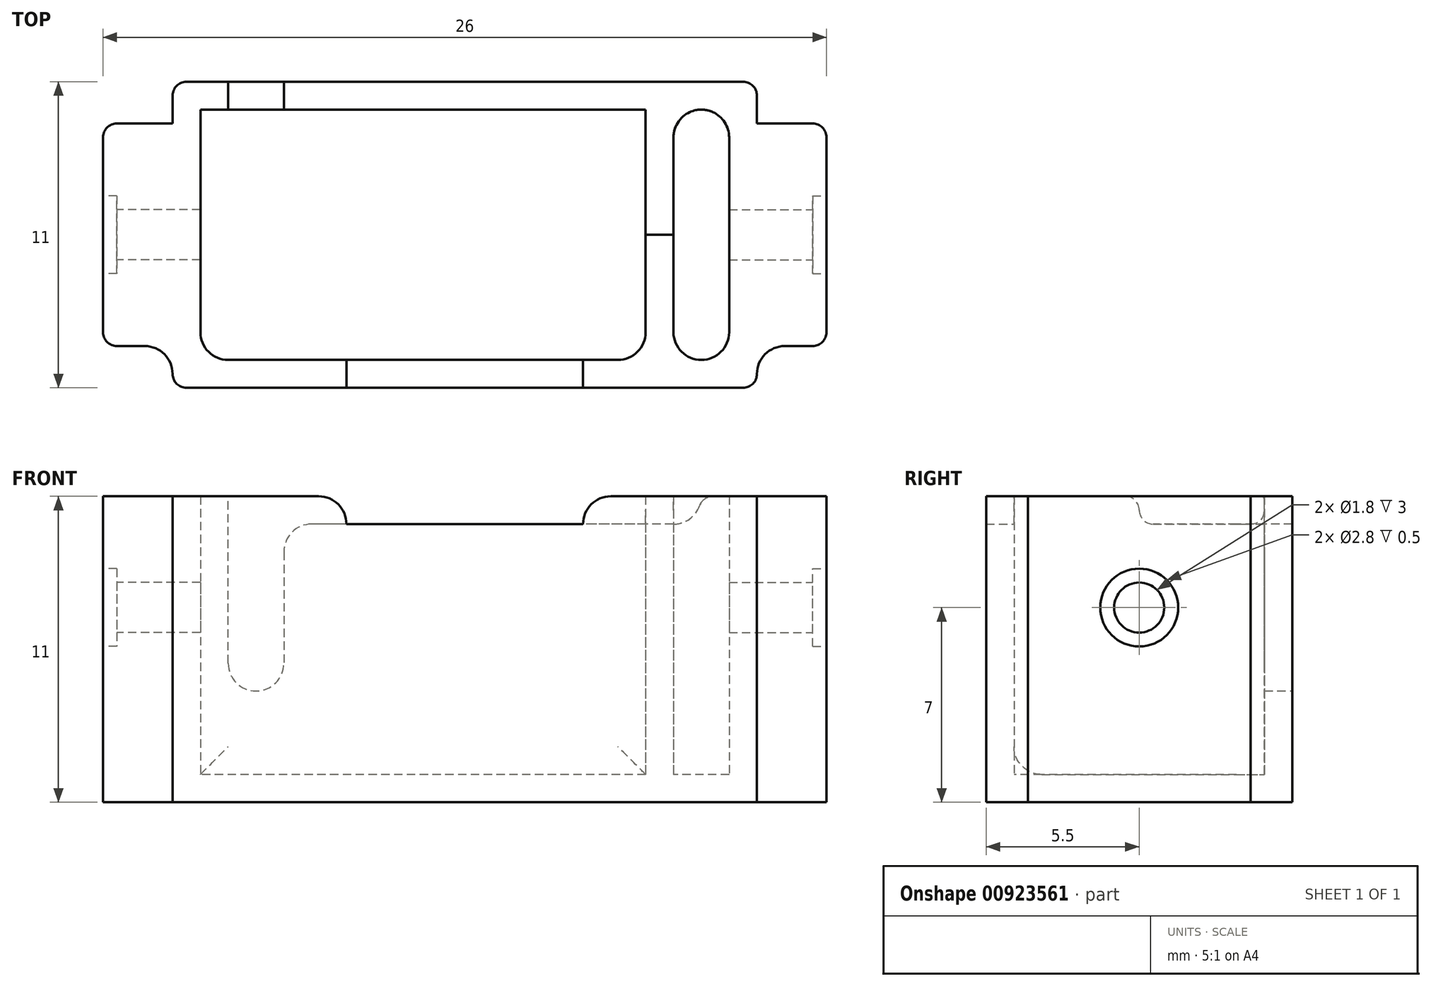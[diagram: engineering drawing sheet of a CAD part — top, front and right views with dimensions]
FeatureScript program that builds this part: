
annotation { "Feature Type Name" : "Feature", "Feature Type Description" : "" }
export const myFeature = defineFeature(function(context is Context, id is Id, definition is map)
    precondition{}
    {
        {
            var Q0;
            Q0=qCreatedBy(makeId("Top.planeOp"),FACE);
            var sketch = newSketch(context, id + "F0", { "sketchPlane" : qUnion([Q0])});
            skLineSegment(sketch, "E0.bottom", {"start": v(9.5, -4.5) * mm, "end": v(-9.5, -4.5) * mm});
            skLineSegment(sketch, "E0.top", {"start": v(9.5, 4.5) * mm, "end": v(-9.5, 4.5) * mm});
            skLineSegment(sketch, "E0.left", {"start": v(9.5, -4.5) * mm, "end": v(9.5, 4.5) * mm});
            skLineSegment(sketch, "E0.right", {"start": v(-9.5, -4.5) * mm, "end": v(-9.5, 4.5) * mm});
            skPoint(sketch, "E0.middle", {"position": v(0, 0) * mm});
            skLineSegment(sketch, "E1.bottom", {"start": v(10.5, -5.5) * mm, "end": v(-10.5, -5.5) * mm});
            skLineSegment(sketch, "E1.top", {"start": v(10.5, 5.5) * mm, "end": v(-10.5, 5.5) * mm});
            skLineSegment(sketch, "E1.left", {"start": v(10.5, -5.5) * mm, "end": v(10.5, 5.5) * mm});
            skLineSegment(sketch, "E1.right", {"start": v(-10.5, -5.5) * mm, "end": v(-10.5, 5.5) * mm});
            skLineSegment(sketch, "E2", {"start": v(9.5, -4.5) * mm, "end": v(6.5, -4.5) * mm});
            skLineSegment(sketch, "E3", {"start": v(6.5, -4.5) * mm, "end": v(6.5, 4.5) * mm});
            skLineSegment(sketch, "E4", {"start": v(13, 0) * mm, "end": v(13, -4) * mm});
            skLineSegment(sketch, "E5", {"start": v(13, -4) * mm, "end": v(10.5, -4) * mm});
            skLineSegment(sketch, "E6", {"start": v(13, 0) * mm, "end": v(13, 4) * mm});
            skLineSegment(sketch, "E7", {"start": v(13, 4) * mm, "end": v(10.5, 4) * mm});
            skLineSegment(sketch, "E8.MirrorCS", {"start": v(-13, 4) * mm, "end": v(-10.5, 4) * mm});
            skLineSegment(sketch, "E9.MirrorCS", {"start": v(-13, 0) * mm, "end": v(-13, 4) * mm});
            skLineSegment(sketch, "E10.MirrorCS", {"start": v(-13, 0) * mm, "end": v(-13, -4) * mm});
            skLineSegment(sketch, "E11.MirrorCS", {"start": v(-13, -4) * mm, "end": v(-10.5, -4) * mm});
            skLineSegment(sketch, "E12", {"start": v(6.5, 4.5) * mm, "end": v(7.5, 4.5) * mm});
            skLineSegment(sketch, "E13", {"start": v(7.5, 4.5) * mm, "end": v(7.5, -4.5) * mm});
            skSolve(sketch);
        }
        {
            var Q0;
            {var subQ3=sQuery(id+"F0.wireOp",EDGE,"E0.left");Q0=makeQuery(id+"F0.imprint","IMPRINT",FACE,{"disambiguationData":[TD([[makeQuery(id+"F0.imprint","IMPRINT",EDGE,{"derivedFrom":subQ3}),-1.0]])]});}
            var Q1;
            {var subQ2=sQuery(id+"F0.wireOp",EDGE,"E0.right");Q1=makeQuery(id+"F0.imprint","IMPRINT",FACE,{"disambiguationData":[TD([[makeQuery(id+"F0.imprint","IMPRINT",EDGE,{"derivedFrom":subQ2}),-1.0]])]});}
            var Q2;
            {var subQ0=sQuery(id+"F0.wireOp",EDGE,"E3");var subQ7=sQuery(id+"F0.wireOp",EDGE,"E0.left");Q2=qUnion([makeQuery(id+"F0.imprint","IMPRINT",FACE,{"disambiguationData":[TD([[makeQuery(id+"F0.imprint","IMPRINT",EDGE,{"derivedFrom":subQ7}),1.0]])]}),makeQuery(id+"F0.imprint","IMPRINT",FACE,{"disambiguationData":[TD([[makeQuery(id+"F0.imprint","IMPRINT",EDGE,{"derivedFrom":subQ0}),-1.0]])]})]);}
            extrude(context, id + "F1", {"entities" : qUnion([Q0, Q1, Q2]), "depth" : 11 * mm, "offsetDistance" : 25 * mm});
        }
        {
            var Q0;
            {var subQ2=sQuery(id+"F0.wireOp",EDGE,"E0.right");Q0=makeQuery(id+"F0.imprint","IMPRINT",FACE,{"disambiguationData":[TD([[makeQuery(id+"F0.imprint","IMPRINT",EDGE,{"derivedFrom":subQ2}),-1.0]])]});}
            var Q1;
            {var subQ0=sQuery(id+"F0.wireOp",EDGE,"E0.left");Q1=makeQuery(id+"F0.imprint","IMPRINT",FACE,{"disambiguationData":[TD([[makeQuery(id+"F0.imprint","IMPRINT",EDGE,{"derivedFrom":subQ0}),1.0]])]});}
            extrude(context, id + "F2", {"entities" : qUnion([Q0, Q1]), "operationType" : NewBodyOperationType.REMOVE, "oppositeDirection" : true, "depth" : -15 * mm, "offsetDistance" : 25 * mm, "hasSecondDirection" : true, "secondDirectionOppositeDirection" : true, "secondDirectionDepth" : -1 * mm});
        }
        {
            var Q0;
            Q0=qCreatedBy(makeId("Front.planeOp"),FACE);
            var sketch = newSketch(context, id + "F3", { "sketchPlane" : qUnion([Q0])});
            skLineSegment(sketch, "E14", {"start": v(0, 0) * mm, "end": v(0, 7) * mm});
            skArc(sketch, "E15", {"start": v(-4.25, 7) * mm, "mid": v(0, 2.75) * mm, "end": v(4.25, 7) * mm});
            skLineSegment(sketch, "E16", {"start": v(4.25, 7) * mm, "end": v(4.25, 11.25) * mm});
            skLineSegment(sketch, "E17", {"start": v(4.25, 11.25) * mm, "end": v(-4.25, 11.25) * mm});
            skLineSegment(sketch, "E18", {"start": v(-4.25, 11.25) * mm, "end": v(-4.25, 7) * mm});
            skLineSegment(sketch, "E19", {"start": v(0, 0) * mm, "end": v(0, 4) * mm});
            skLineSegment(sketch, "E20", {"start": v(-6.5, 11) * mm, "end": v(8.5, 11) * mm});
            skLineSegment(sketch, "E21", {"start": v(8.5, 11) * mm, "end": v(8.5, 10) * mm});
            skLineSegment(sketch, "E22", {"start": v(8.5, 10) * mm, "end": v(-6.5, 10) * mm});
            skLineSegment(sketch, "E23", {"start": v(-6.5, 10) * mm, "end": v(-6.5, 4) * mm});
            skLineSegment(sketch, "E24", {"start": v(-6.5, 4) * mm, "end": v(-8.5, 4) * mm});
            skLineSegment(sketch, "E25", {"start": v(-8.5, 4) * mm, "end": v(-8.5, 11) * mm});
            skLineSegment(sketch, "E26", {"start": v(-8.5, 11) * mm, "end": v(-6.5, 11) * mm});
            skSolve(sketch);
        }
        {
            var Q0;
            {var subQ2=sQuery(id+"F3.wireOp",EDGE,"E16");Q0=makeQuery(id+"F3.imprint","IMPRINT",FACE,{"disambiguationData":[TD([[makeQuery(id+"F3.imprint","IMPRINT",EDGE,{"derivedFrom":subQ2}),1.0]])]});}
            extrude(context, id + "F4", {"entities" : qUnion([Q0]), "operationType" : NewBodyOperationType.REMOVE, "oppositeDirection" : true, "depth" : -10 * mm, "offsetDistance" : 25 * mm});
        }
        {
            var Q0;
            Q0=makeQuery(id+"F0.imprint","IMPRINT",FACE,{"disambiguationData":[TD([[makeQuery(id+"F0.imprint","IMPRINT",EDGE,{"derivedFrom":sQuery(id+"F0.wireOp",EDGE,"E4")}),-1.0]])]});
            var Q1;
            {var subQ0=sQuery(id+"F0.wireOp",EDGE,"E8.MirrorCS");Q1=makeQuery(id+"F0.imprint","IMPRINT",FACE,{"disambiguationData":[TD([[makeQuery(id+"F0.imprint","IMPRINT",EDGE,{"derivedFrom":subQ0}),-1.0]])]});}
            extrude(context, id + "F5", {"entities" : qUnion([Q0, Q1]), "operationType" : NewBodyOperationType.ADD, "depth" : 11 * mm, "offsetDistance" : 25 * mm});
        }
        {
            var Q0;
            {var subQ1=sQuery(id+"F3.wireOp",EDGE,"BxqcTW8r-oT3u-ynJ6-vhvX-lELADfX308RM");Q0=makeQuery(id+"F3.imprint","IMPRINT",FACE,{"disambiguationData":[TD([[makeQuery(id+"F3.imprint","IMPRINT",EDGE,{"derivedFrom":subQ1}),-1.0]])]});}
            var Q1;
            {var subQ5=sQuery(id+"F3.wireOp",EDGE,"E21");Q1=makeQuery(id+"F3.imprint","IMPRINT",FACE,{"disambiguationData":[TD([[makeQuery(id+"F3.imprint","IMPRINT",EDGE,{"derivedFrom":subQ5}),-1.0]])]});}
            var Q2;
            {var subQ0=sQuery(id+"F3.wireOp",EDGE,"E22");var subQ1=sQuery(id+"F3.wireOp",EDGE,"E16");var subQ2=makeQuery(id+"F3.imprint","INTERSECT",VERTEX,{"derivedFrom":[subQ1,subQ0]});Q2=makeQuery(id+"F3.imprint","IMPRINT",FACE,{"disambiguationData":[TD([[makeQuery(id+"F3.imprint","IMPRINT",EDGE,{"disambiguationData":[TD([[subQ2,-1.0]])],"derivedFrom":subQ1}),1.0]])]});}
            var Q3;
            {var subQ0=sQuery(id+"F3.wireOp",EDGE,"E23");Q3=makeQuery(id+"F3.imprint","IMPRINT",FACE,{"disambiguationData":[TD([[makeQuery(id+"F3.imprint","IMPRINT",EDGE,{"derivedFrom":subQ0}),-1.0]])]});}
            extrude(context, id + "F6", {"entities" : qUnion([Q0, Q1, Q2, Q3]), "operationType" : NewBodyOperationType.REMOVE, "oppositeDirection" : true, "depth" : 6 * mm, "offsetDistance" : 25 * mm});
        }
        {
            var Q0;
            Q0=makeQuery(id+"F5.opExtrude","SWEPT_EDGE",EDGE,{"disambiguationData":[OSD([sQuery(id+"F0.wireOp",EDGE,"E1.left"),sQuery(id+"F0.wireOp",EDGE,"E5")])]});
            var Q1;
            Q1=makeQuery(id+"F5.opExtrude","SWEPT_EDGE",EDGE,{"disambiguationData":[OSD([sQuery(id+"F0.wireOp",EDGE,"E1.left"),sQuery(id+"F0.wireOp",EDGE,"E7")])]});
            var Q2;
            Q2=makeQuery(id+"F5.opExtrude","SWEPT_EDGE",EDGE,{"disambiguationData":[OSD([sQuery(id+"F0.wireOp",EDGE,"E1.right"),sQuery(id+"F0.wireOp",EDGE,"E8.MirrorCS")])]});
            var Q3;
            Q3=makeQuery(id+"F5.opExtrude","SWEPT_EDGE",EDGE,{"disambiguationData":[OSD([sQuery(id+"F0.wireOp",EDGE,"E1.right"),sQuery(id+"F0.wireOp",EDGE,"E11.MirrorCS")])]});
            var Q4;
            Q4=makeQuery(id+"F4.boolean.opBoolean","INTERSECT",EDGE,{"derivedFrom":[makeQuery(id+"F1.opExtrude","CAP_FACE",FACE,{"disambiguationData":[OSD([sQuery(id+"F0.wireOp",EDGE,"E1.bottom"),sQuery(id+"F0.wireOp",EDGE,"E1.top"),sQuery(id+"F0.wireOp",EDGE,"E1.left"),sQuery(id+"F0.wireOp",EDGE,"E1.right")])],"isStart":false}),makeQuery(id+"F4.opExtrude","SWEPT_FACE",FACE,{"disambiguationData":[OSD([sQuery(id+"F3.wireOp",EDGE,"E18")])]})]});
            var Q5;
            Q5=makeQuery(id+"F4.boolean.opBoolean","INTERSECT",EDGE,{"derivedFrom":[makeQuery(id+"F1.opExtrude","CAP_FACE",FACE,{"disambiguationData":[OSD([sQuery(id+"F0.wireOp",EDGE,"E1.bottom"),sQuery(id+"F0.wireOp",EDGE,"E1.top"),sQuery(id+"F0.wireOp",EDGE,"E1.left"),sQuery(id+"F0.wireOp",EDGE,"E1.right")])],"isStart":false}),makeQuery(id+"F4.opExtrude","SWEPT_FACE",FACE,{"disambiguationData":[OSD([sQuery(id+"F3.wireOp",EDGE,"E16")])]})]});
            var Q6;
            Q6=makeQuery(id+"F6.boolean.opBoolean","COPY",EDGE,{"derivedFrom":makeQuery(id+"F6.opExtrude","SWEPT_EDGE",EDGE,{"disambiguationData":[OSD([sQuery(id+"F3.wireOp",EDGE,"E24"),sQuery(id+"F3.wireOp",EDGE,"E25")])]})});
            var Q7;
            Q7=makeQuery(id+"F6.boolean.opBoolean","COPY",EDGE,{"derivedFrom":makeQuery(id+"F6.opExtrude","SWEPT_EDGE",EDGE,{"disambiguationData":[OSD([sQuery(id+"F3.wireOp",EDGE,"E23"),sQuery(id+"F3.wireOp",EDGE,"E24")])]})});
            var Q8;
            Q8=makeQuery(id+"F6.boolean.opBoolean","COPY",EDGE,{"derivedFrom":makeQuery(id+"F6.opExtrude","SWEPT_EDGE",EDGE,{"disambiguationData":[OSD([sQuery(id+"F3.wireOp",EDGE,"E25"),sQuery(id+"F3.wireOp",EDGE,"E26")])]})});
            var Q9;
            Q9=makeQuery(id+"F6.boolean.opBoolean","COPY",EDGE,{"derivedFrom":makeQuery(id+"F6.opExtrude","SWEPT_EDGE",EDGE,{"disambiguationData":[OSD([sQuery(id+"F3.wireOp",EDGE,"E22"),sQuery(id+"F3.wireOp",EDGE,"E23")])]})});
            var Q10;
            Q10=makeQuery(id+"F6.boolean.opBoolean","COPY",EDGE,{"derivedFrom":makeQuery(id+"F6.opExtrude","SWEPT_EDGE",EDGE,{"disambiguationData":[OSD([sQuery(id+"F3.wireOp",EDGE,"E21"),sQuery(id+"F3.wireOp",EDGE,"E22")])]})});
            fillet(context, id + "F7", {"entities" : qUnion([Q0, Q1, Q2, Q3, Q4, Q5, Q6, Q7, Q8, Q9, Q10]), "radius" : 1 * mm, "tangentPropagation" : true, "allowEdgeOverflow" : false});
        }
        {
            var Q0;
            {var subQ1=sQuery(id+"F0.wireOp",EDGE,"E1.left");var subQ3=sQuery(id+"F0.wireOp",EDGE,"E1.top");var subQ6=sQuery(id+"F0.wireOp",EDGE,"E1.bottom");var subQ7=sQuery(id+"F0.wireOp",EDGE,"E6");var subQ8=sQuery(id+"F0.wireOp",EDGE,"E4");var subQ10=sQuery(id+"F0.wireOp",EDGE,"E5");var subQ11=sQuery(id+"F0.wireOp",EDGE,"E7");var subQ12=sQuery(id+"F3.wireOp",EDGE,"E22");var subQ13=sQuery(id+"F3.wireOp",EDGE,"E21");var subQ14=sQuery(id+"F0.wireOp",EDGE,"E1.right");Q0=makeQuery(id+"F7.opFillet","BLEND_EDGE",EDGE,{"blendedFrom":[makeQuery(id+"F6.boolean.opBoolean","COPY",EDGE,{"derivedFrom":makeQuery(id+"F6.opExtrude","SWEPT_EDGE",EDGE,{"disambiguationData":[OSD([subQ13,subQ12])]})}),makeQuery(id+"F6.boolean.opBoolean","SPLIT",FACE,{"disambiguationData":[TD([makeQuery(id+"F1.opExtrude","SWEPT_FACE",FACE,{"disambiguationData":[OSD([subQ1])]})])],"derivedFrom":makeQuery(id+"F5.boolean.opBoolean","MERGE",FACE,{"derivedFrom":[makeQuery(id+"F1.opExtrude","CAP_FACE",FACE,{"disambiguationData":[OSD([subQ6,subQ3,subQ1,subQ14])],"isStart":false}),makeQuery(id+"F5.opExtrude","CAP_FACE",FACE,{"disambiguationData":[OSD([subQ1,subQ8,subQ10,subQ7,subQ11])],"isStart":false}),makeQuery(id+"F5.opExtrude","CAP_FACE",FACE,{"disambiguationData":[OSD([subQ14,sQuery(id+"F0.wireOp",EDGE,"E8.MirrorCS"),sQuery(id+"F0.wireOp",EDGE,"E9.MirrorCS"),sQuery(id+"F0.wireOp",EDGE,"E10.MirrorCS"),sQuery(id+"F0.wireOp",EDGE,"E11.MirrorCS")])],"isStart":false})]})})],"blendedInto":[makeQuery(id+"F6.boolean.opBoolean","SPLIT",FACE,{"disambiguationData":[TD([makeQuery(id+"F1.opExtrude","SWEPT_FACE",FACE,{"disambiguationData":[OSD([subQ1])]})])],"derivedFrom":makeQuery(id+"F5.boolean.opBoolean","MERGE",FACE,{"derivedFrom":[makeQuery(id+"F1.opExtrude","CAP_FACE",FACE,{"disambiguationData":[OSD([subQ6,subQ3,subQ1,subQ14])],"isStart":false}),makeQuery(id+"F5.opExtrude","CAP_FACE",FACE,{"disambiguationData":[OSD([subQ1,subQ8,subQ10,subQ7,subQ11])],"isStart":false}),makeQuery(id+"F5.opExtrude","CAP_FACE",FACE,{"disambiguationData":[OSD([subQ14,sQuery(id+"F0.wireOp",EDGE,"E8.MirrorCS"),sQuery(id+"F0.wireOp",EDGE,"E9.MirrorCS"),sQuery(id+"F0.wireOp",EDGE,"E10.MirrorCS"),sQuery(id+"F0.wireOp",EDGE,"E11.MirrorCS")])],"isStart":false})]})})]});}
            var Q1;
            Q1=makeQuery(id+"F6.boolean.opBoolean","COPY",EDGE,{"derivedFrom":makeQuery(id+"F6.opExtrude","CAP_EDGE",EDGE,{"disambiguationData":[OSD([sQuery(id+"F3.wireOp",EDGE,"E22")])],"isStart":true})});
            var Q2;
            Q2=makeQuery(id+"F6.boolean.opBoolean","COPY",EDGE,{"derivedFrom":makeQuery(id+"F6.opExtrude","CAP_EDGE",EDGE,{"disambiguationData":[OSD([sQuery(id+"F3.wireOp",EDGE,"E20"),sQuery(id+"F3.wireOp",EDGE,"E26")])],"isStart":true})});
            var Q3;
            Q3=makeQuery(id+"F5.opExtrude","SWEPT_EDGE",EDGE,{"disambiguationData":[OSD([sQuery(id+"F0.wireOp",EDGE,"E4"),sQuery(id+"F0.wireOp",EDGE,"E5")])]});
            var Q4;
            Q4=makeQuery(id+"F5.opExtrude","SWEPT_EDGE",EDGE,{"disambiguationData":[OSD([sQuery(id+"F0.wireOp",EDGE,"E6"),sQuery(id+"F0.wireOp",EDGE,"E7")])]});
            var Q5;
            Q5=makeQuery(id+"F5.opExtrude","SWEPT_EDGE",EDGE,{"disambiguationData":[OSD([sQuery(id+"F0.wireOp",EDGE,"E8.MirrorCS"),sQuery(id+"F0.wireOp",EDGE,"E9.MirrorCS")])]});
            var Q6;
            Q6=makeQuery(id+"F5.opExtrude","SWEPT_EDGE",EDGE,{"disambiguationData":[OSD([sQuery(id+"F0.wireOp",EDGE,"E10.MirrorCS"),sQuery(id+"F0.wireOp",EDGE,"E11.MirrorCS")])]});
            var Q7;
            Q7=makeQuery(id+"F1.opExtrude","SWEPT_EDGE",EDGE,{"disambiguationData":[OSD([sQuery(id+"F0.wireOp",EDGE,"E1.bottom"),sQuery(id+"F0.wireOp",EDGE,"E1.right")])]});
            var Q8;
            Q8=makeQuery(id+"F1.opExtrude","SWEPT_EDGE",EDGE,{"disambiguationData":[OSD([sQuery(id+"F0.wireOp",EDGE,"E1.top"),sQuery(id+"F0.wireOp",EDGE,"E1.right")])]});
            var Q9;
            Q9=makeQuery(id+"F1.opExtrude","SWEPT_EDGE",EDGE,{"disambiguationData":[OSD([sQuery(id+"F0.wireOp",EDGE,"E1.top"),sQuery(id+"F0.wireOp",EDGE,"E1.left")])]});
            var Q10;
            Q10=makeQuery(id+"F1.opExtrude","SWEPT_EDGE",EDGE,{"disambiguationData":[OSD([sQuery(id+"F0.wireOp",EDGE,"E1.bottom"),sQuery(id+"F0.wireOp",EDGE,"E1.left")])]});
            fillet(context, id + "F8", {"entities" : qUnion([Q0, Q1, Q2, Q3, Q4, Q5, Q6, Q7, Q8, Q9, Q10]), "radius" : 0.5 * mm, "tangentPropagation" : true, "allowEdgeOverflow" : false});
        }
        {
            var Q0;
            Q0=makeQuery(id+"F2.boolean.opBoolean","COPY",EDGE,{"derivedFrom":makeQuery(id+"F2.opExtrude","SWEPT_EDGE",EDGE,{"disambiguationData":[OSD([sQuery(id+"F0.wireOp",EDGE,"E0.bottom"),sQuery(id+"F0.wireOp",EDGE,"E0.right")])]})});
            var Q1;
            Q1=makeQuery(id+"F2.boolean.opBoolean","COPY",EDGE,{"derivedFrom":makeQuery(id+"F2.opExtrude","SWEPT_EDGE",EDGE,{"disambiguationData":[OSD([sQuery(id+"F0.wireOp",EDGE,"E0.bottom"),sQuery(id+"F0.wireOp",EDGE,"E3")])]})});
            var Q2;
            {var subQ0=sQuery(id+"F0.wireOp",EDGE,"E0.bottom");Q2=makeQuery(id+"F2.boolean.opBoolean","COPY",EDGE,{"derivedFrom":makeQuery(id+"F2.opExtrude","CAP_EDGE",EDGE,{"disambiguationData":[OSD([subQ0]),TDD([makeQuery(id+"F0.imprint","IMPRINT",EDGE,{"disambiguationData":[TD([[makeQuery(id+"F0.imprint","INTERSECT",VERTEX,{"derivedFrom":[subQ0,sQuery(id+"F0.wireOp",EDGE,"E3")]}),-1.0]])],"derivedFrom":subQ0})])],"isStart":true})});}
            var Q3;
            Q3=makeQuery(id+"F2.boolean.opBoolean","COPY",EDGE,{"derivedFrom":makeQuery(id+"F2.opExtrude","SWEPT_EDGE",EDGE,{"disambiguationData":[OSD([sQuery(id+"F0.wireOp",EDGE,"E0.bottom"),sQuery(id+"F0.wireOp",EDGE,"E13")])]})});
            var Q4;
            Q4=makeQuery(id+"F2.boolean.opBoolean","COPY",EDGE,{"derivedFrom":makeQuery(id+"F2.opExtrude","SWEPT_EDGE",EDGE,{"disambiguationData":[OSD([sQuery(id+"F0.wireOp",EDGE,"E0.bottom"),sQuery(id+"F0.wireOp",EDGE,"E0.left")])]})});
            var Q5;
            Q5=makeQuery(id+"F2.boolean.opBoolean","COPY",EDGE,{"derivedFrom":makeQuery(id+"F2.opExtrude","SWEPT_EDGE",EDGE,{"disambiguationData":[OSD([sQuery(id+"F0.wireOp",EDGE,"E0.top"),sQuery(id+"F0.wireOp",EDGE,"E13")])]})});
            var Q6;
            Q6=makeQuery(id+"F2.boolean.opBoolean","COPY",EDGE,{"derivedFrom":makeQuery(id+"F2.opExtrude","SWEPT_EDGE",EDGE,{"disambiguationData":[OSD([sQuery(id+"F0.wireOp",EDGE,"E0.top"),sQuery(id+"F0.wireOp",EDGE,"E0.left")])]})});
            fillet(context, id + "F9", {"entities" : qUnion([Q0, Q1, Q2, Q3, Q4, Q5, Q6]), "radius" : 1 * mm, "tangentPropagation" : true, "allowEdgeOverflow" : false});
        }
        {
            var Q0;
            Q0=makeQuery(id+"F5.opExtrude","SWEPT_FACE",FACE,{"disambiguationData":[OSD([sQuery(id+"F0.wireOp",EDGE,"E4"),sQuery(id+"F0.wireOp",EDGE,"E6")])]});
            var sketch = newSketch(context, id + "F10", { "sketchPlane" : qUnion([Q0])});
            skLineSegment(sketch, "E27", {"start": v(0, 0) * mm, "end": v(0, 7) * mm});
            skPoint(sketch, "E28", {"position": v(0, 7) * mm});
            skSolve(sketch);
        }
        {
            var Q0;
            Q0=sQuery(id+"F10.wireOp",VERTEX,"E28");
            var Q1;
            Q1=makeQuery(id+"F1.opExtrude","SWEPT_BODY",BODY,{"disambiguationData":[OSD([sQuery(id+"F0.wireOp",EDGE,"E1.bottom"),sQuery(id+"F0.wireOp",EDGE,"E1.top"),sQuery(id+"F0.wireOp",EDGE,"E1.left"),sQuery(id+"F0.wireOp",EDGE,"E1.right")])]});
            hole(context, id + "F11", {"style" : HoleStyle.C_BORE, "endStyle" : HoleEndStyle.BLIND, "holeDiameter" : 1.8 * mm, "cBoreDiameter" : 2.8 * mm, "cBoreDepth" : 0.5 * mm, "majorDiameter" : 5 * mm, "holeDepth" : 4 * mm, "isTappedThrough" : true, "tappedDepth" : 12 * mm, "tapClearance" : 3, "locations" : qUnion([Q0]), "scope" : qUnion([Q1])});
        }
        {
            var Q0;
            Q0=makeQuery(id+"F5.opExtrude","SWEPT_FACE",FACE,{"disambiguationData":[OSD([sQuery(id+"F0.wireOp",EDGE,"E9.MirrorCS"),sQuery(id+"F0.wireOp",EDGE,"E10.MirrorCS")])]});
            var sketch = newSketch(context, id + "F12", { "sketchPlane" : qUnion([Q0])});
            skLineSegment(sketch, "E29", {"start": v(0, 0) * mm, "end": v(0, 7) * mm});
            skPoint(sketch, "E30", {"position": v(0, 7) * mm});
            skSolve(sketch);
        }
        {
            var Q0;
            Q0=sQuery(id+"F12.wireOp",VERTEX,"E30");
            var Q1;
            Q1=makeQuery(id+"F1.opExtrude","SWEPT_BODY",BODY,{"disambiguationData":[OSD([sQuery(id+"F0.wireOp",EDGE,"E1.bottom"),sQuery(id+"F0.wireOp",EDGE,"E1.top"),sQuery(id+"F0.wireOp",EDGE,"E1.left"),sQuery(id+"F0.wireOp",EDGE,"E1.right")])]});
            hole(context, id + "F13", {"style" : HoleStyle.C_BORE, "endStyle" : HoleEndStyle.BLIND, "holeDiameter" : 1.8 * mm, "cBoreDiameter" : 2.8 * mm, "cBoreDepth" : 0.5 * mm, "majorDiameter" : 5 * mm, "holeDepth" : 4 * mm, "isTappedThrough" : true, "tappedDepth" : 12 * mm, "tapClearance" : 3, "locations" : qUnion([Q0]), "scope" : qUnion([Q1])});
        }
    });
